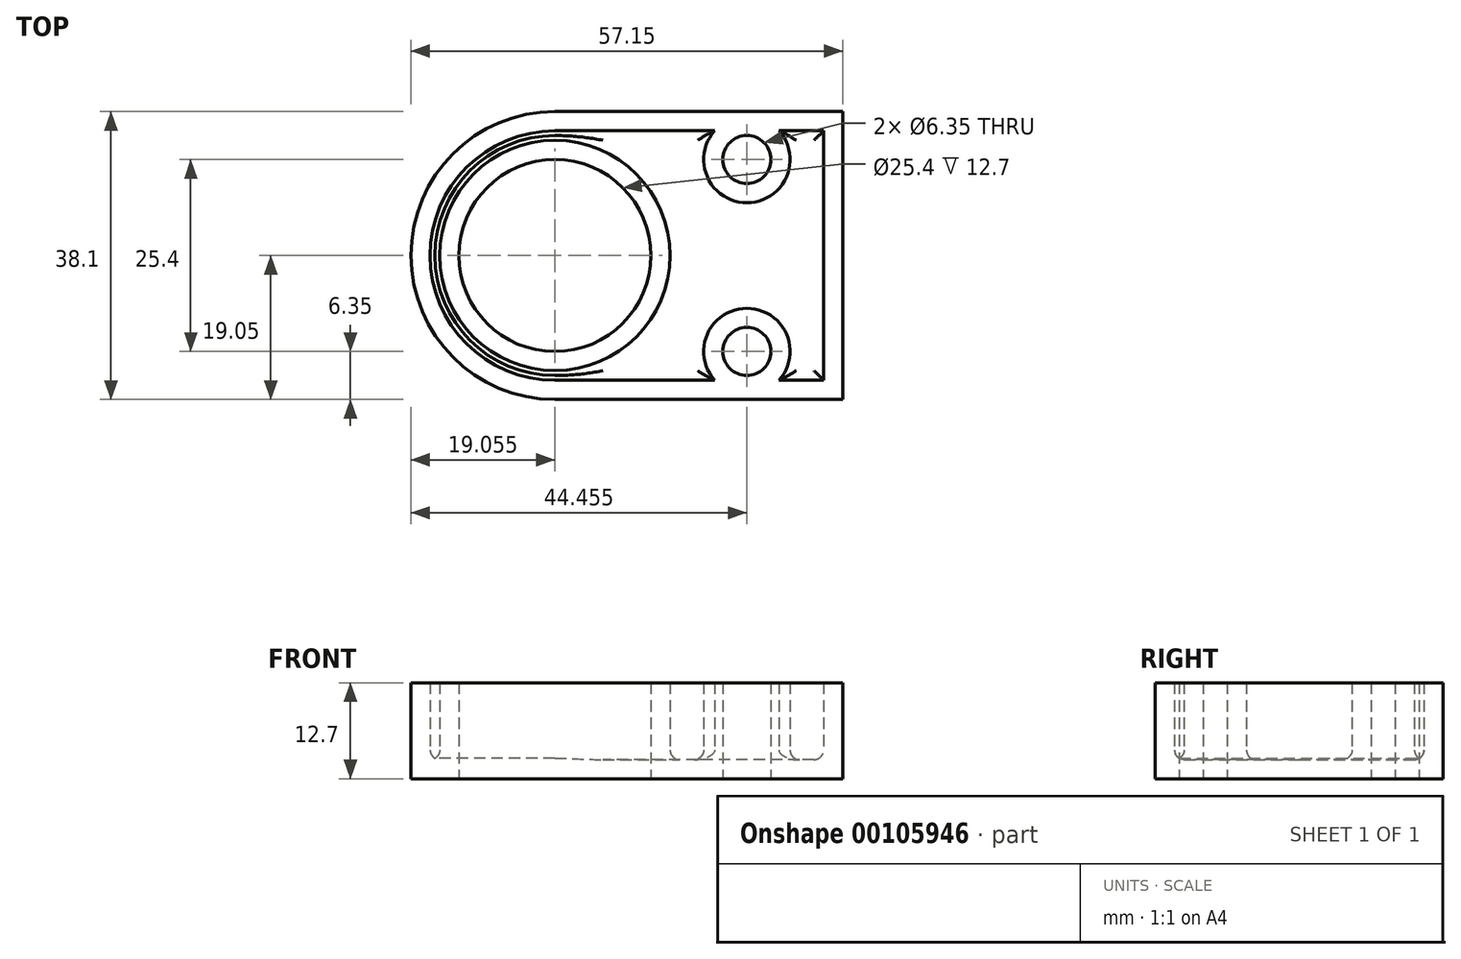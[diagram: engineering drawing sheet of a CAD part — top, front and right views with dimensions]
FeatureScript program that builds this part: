
annotation { "Feature Type Name" : "Feature", "Feature Type Description" : "" }
export const myFeature = defineFeature(function(context is Context, id is Id, definition is map)
    precondition{}
    {
        {
            var Q0;
            Q0=qCreatedBy(makeId("Top.planeOp"),FACE);
            var sketch = newSketch(context, id + "F0", { "sketchPlane" : qUnion([Q0])});
            skLineSegment(sketch, "E0.bottom", {"start": v(28.57, 19.05) * mm, "end": v(-9.53, 19.05) * mm});
            skLineSegment(sketch, "E0.top", {"start": v(28.58, -19.05) * mm, "end": v(-9.53, -19.05) * mm});
            skLineSegment(sketch, "E0.left", {"start": v(28.57, 19.05) * mm, "end": v(28.58, -19.05) * mm});
            skPoint(sketch, "E0.middle", {"position": v(0, 0) * mm});
            skArc(sketch, "E1", {"start": v(-9.53, 19.05) * mm, "mid": v(-28.57, 0) * mm, "end": v(-9.53, -19.05) * mm});
            skPoint(sketch, "E1.first.point", {"position": v(-9.53, 19.05) * mm});
            skPoint(sketch, "E1.second.point", {"position": v(-9.53, -19.05) * mm});
            skPoint(sketch, "E1.third.point", {"position": v(-28.58, 0) * mm});
            skPoint(sketch, "E2.orphan", {"position": v(-28.58, 19.05) * mm});
            skPoint(sketch, "E3.orphan", {"position": v(-28.57, -19.05) * mm});
            skCircle(sketch, "E4", {"center": v(-9.53, 0) * mm, "radius": 12.7 * mm});
            skLineSegment(sketch, "E5", {"start": v(28.58, 12.7) * mm, "end": v(-23.72, 12.7) * mm, "construction": true});
            skLineSegment(sketch, "E6", {"start": v(28.58, -12.7) * mm, "end": v(-23.72, -12.7) * mm, "construction": true});
            skLineSegment(sketch, "E7", {"start": v(15.88, 19.05) * mm, "end": v(15.88, -19.05) * mm, "construction": true});
            skCircle(sketch, "E8", {"center": v(15.88, 12.7) * mm, "radius": 3.18 * mm});
            skCircle(sketch, "E9", {"center": v(15.88, -12.7) * mm, "radius": 3.18 * mm});
            skSolve(sketch);
        }
        {
            var Q0;
            Q0 = qSketchRegion(id + "F0", true);
            extrude(context, id + "F1", {"entities" : qUnion([Q0]), "depth" : 12.7 * mm});
        }
        {
            var Q0;
            Q0=makeQuery(id+"F1.opExtrude","CAP_FACE",FACE,{"disambiguationData":[OSD([sQuery(id+"F0.wireOp",EDGE,"E0.bottom"),sQuery(id+"F0.wireOp",EDGE,"E0.top"),sQuery(id+"F0.wireOp",EDGE,"E0.left"),sQuery(id+"F0.wireOp",EDGE,"E1"),sQuery(id+"F0.wireOp",EDGE,"E4"),sQuery(id+"F0.wireOp",EDGE,"E8"),sQuery(id+"F0.wireOp",EDGE,"E9")])],"isStart":false});
            shell(context, id + "F2", {"entities" : qUnion([Q0]), "thickness" : 2.54 * mm});
        }
        {
            var Q0;
            {var subQ0=sQuery(id+"F0.wireOp",EDGE,"E9");var subQ1=sQuery(id+"F0.wireOp",EDGE,"E8");var subQ2=sQuery(id+"F0.wireOp",EDGE,"E4");var subQ3=sQuery(id+"F0.wireOp",EDGE,"E1");var subQ4=sQuery(id+"F0.wireOp",EDGE,"E0.left");var subQ5=sQuery(id+"F0.wireOp",EDGE,"E0.top");var subQ6=sQuery(id+"F0.wireOp",EDGE,"E0.bottom");Q0=makeQuery(id+"F2.opShell","OFFSET_FACE",FACE,{"disambiguationData":[OSD([subQ6,subQ5,subQ4,subQ3,subQ2,subQ1,subQ0]),TDD([makeQuery(id+"F1.opExtrude","CAP_FACE",FACE,{"disambiguationData":[OSD([subQ6,subQ5,subQ4,subQ3,subQ2,subQ1,subQ0])],"isStart":true})])]});}
            fillet(context, id + "F3", {"entities" : qUnion([Q0]), "radius" : 1.27 * mm, "tangentPropagation" : true, "allowEdgeOverflow" : false});
        }
    });
